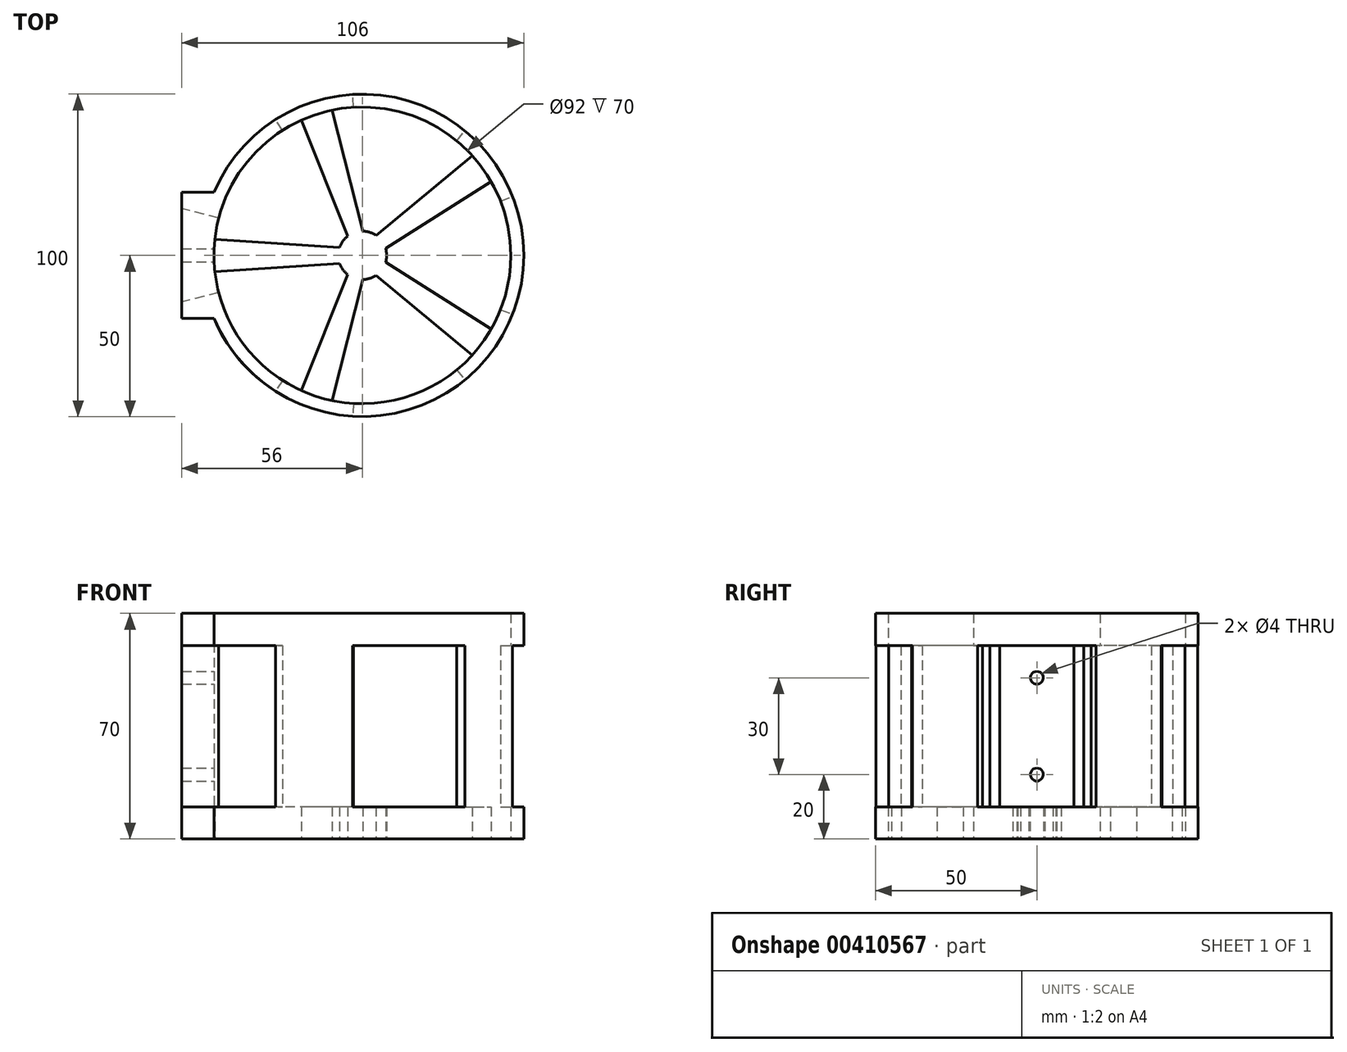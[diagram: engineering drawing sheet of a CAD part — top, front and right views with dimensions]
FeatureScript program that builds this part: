
annotation { "Feature Type Name" : "Feature", "Feature Type Description" : "" }
export const myFeature = defineFeature(function(context is Context, id is Id, definition is map)
    precondition{}
    {
        {
            var Q0;
            Q0=qCreatedBy(makeId("Top.planeOp"),FACE);
            var sketch = newSketch(context, id + "F0", { "sketchPlane" : qUnion([Q0])});
            skArc(sketch, "E0", {"start": v(-46, -19.6) * mm, "mid": v(50, 0) * mm, "end": v(-46, 19.6) * mm});
            skLineSegment(sketch, "E1", {"start": v(-46, -19.6) * mm, "end": v(-46, 19.6) * mm, "construction": true});
            skLineSegment(sketch, "E2", {"start": v(-46, 19.6) * mm, "end": v(-56, 19.6) * mm});
            skLineSegment(sketch, "E3", {"start": v(-46, -19.6) * mm, "end": v(-56, -19.6) * mm});
            skLineSegment(sketch, "E4", {"start": v(-56, -19.6) * mm, "end": v(-56, 19.6) * mm});
            skCircle(sketch, "E5", {"center": v(0, 0) * mm, "radius": 46 * mm});
            skSolve(sketch);
        }
        {
            var Q0;
            Q0=qSketchRegion(id+"F0",true);
            extrude(context, id + "F1", {"entities" : qUnion([Q0]), "depth" : 70 * mm});
        }
        {
            var Q0;
            Q0=makeQuery(id+"F1.opExtrude","CAP_FACE",FACE,{"disambiguationData":[OSD([sQuery(id+"F0.wireOp",EDGE,"E0"),sQuery(id+"F0.wireOp",EDGE,"E2"),sQuery(id+"F0.wireOp",EDGE,"E3"),sQuery(id+"F0.wireOp",EDGE,"E4"),sQuery(id+"F0.wireOp",EDGE,"E5")])],"isStart":true});
            var sketch = newSketch(context, id + "F2", { "sketchPlane" : qUnion([Q0])});
            skPoint(sketch, "E6", {"position": v(0, 0) * mm});
            skCircle(sketch, "E7", {"center": v(0, 0) * mm, "radius": 7.5 * mm});
            skLineSegment(sketch, "E8", {"start": v(-4.56, 5.95) * mm, "end": v(-18.89, 41.94) * mm});
            skLineSegment(sketch, "E9", {"start": v(0.2, 7.5) * mm, "end": v(-9.38, 45.03) * mm});
            skLineSegment(sketch, "E10", {"start": v(-18.89, 41.94) * mm, "end": v(-9.38, 45.03) * mm, "construction": true});
            skLineSegment(sketch, "E11", {"start": v(-4.56, 5.95) * mm, "end": v(0.2, 7.5) * mm, "construction": true});
            skLineSegment(sketch, "E12.1.0", {"start": v(-7.07, -2.5) * mm, "end": v(-45.73, -5) * mm});
            skLineSegment(sketch, "E12.1.1", {"start": v(-7.07, 2.5) * mm, "end": v(-45.73, 5) * mm});
            skLineSegment(sketch, "E12.1.2", {"start": v(-45.73, -5) * mm, "end": v(-45.73, 5) * mm, "construction": true});
            skLineSegment(sketch, "E12.1.3", {"start": v(-7.07, -2.5) * mm, "end": v(-7.07, 2.5) * mm, "construction": true});
            skLineSegment(sketch, "E12.2.0", {"start": v(0.2, -7.5) * mm, "end": v(-9.38, -45.03) * mm});
            skLineSegment(sketch, "E12.2.1", {"start": v(-4.56, -5.95) * mm, "end": v(-18.89, -41.94) * mm});
            skLineSegment(sketch, "E12.2.2", {"start": v(-9.38, -45.03) * mm, "end": v(-18.89, -41.94) * mm, "construction": true});
            skLineSegment(sketch, "E12.2.3", {"start": v(0.2, -7.5) * mm, "end": v(-4.56, -5.95) * mm, "construction": true});
            skLineSegment(sketch, "E13.1.3.0", {"start": v(7.2, -2.13) * mm, "end": v(39.93, -22.83) * mm});
            skLineSegment(sketch, "E13.3.3.0", {"start": v(4.25, -6.18) * mm, "end": v(34.06, -30.92) * mm});
            skLineSegment(sketch, "E13.6.3.0", {"start": v(39.93, -22.83) * mm, "end": v(34.06, -30.92) * mm, "construction": true});
            skLineSegment(sketch, "E13.9.3.0", {"start": v(7.2, -2.13) * mm, "end": v(4.25, -6.18) * mm, "construction": true});
            skLineSegment(sketch, "E13.1.4.0", {"start": v(4.25, 6.18) * mm, "end": v(34.06, 30.92) * mm});
            skLineSegment(sketch, "E13.3.4.0", {"start": v(7.2, 2.13) * mm, "end": v(39.93, 22.83) * mm});
            skLineSegment(sketch, "E13.6.4.0", {"start": v(34.06, 30.92) * mm, "end": v(39.93, 22.83) * mm, "construction": true});
            skLineSegment(sketch, "E13.9.4.0", {"start": v(4.25, 6.18) * mm, "end": v(7.2, 2.13) * mm, "construction": true});
            skSolve(sketch);
        }
        {
            var Q0;
            Q0=qSketchRegion(id+"F2",true);
            var Q1;
            {var subQ0=sQuery(id+"F2.wireOp",EDGE,"E12.1.0");Q1=makeQuery(id+"F2.imprint","IMPRINT",FACE,{"disambiguationData":[TD([[makeQuery(id+"F2.imprint","IMPRINT",EDGE,{"derivedFrom":subQ0}),-1.0]])]});}
            var Q2;
            {var subQ0=sQuery(id+"F2.wireOp",EDGE,"E8");Q2=makeQuery(id+"F2.imprint","IMPRINT",FACE,{"disambiguationData":[TD([[makeQuery(id+"F2.imprint","IMPRINT",EDGE,{"derivedFrom":subQ0}),-1.0]])]});}
            var Q3;
            {var subQ0=sQuery(id+"F2.wireOp",EDGE,"E13.1.4.0");Q3=makeQuery(id+"F2.imprint","IMPRINT",FACE,{"disambiguationData":[TD([[makeQuery(id+"F2.imprint","IMPRINT",EDGE,{"derivedFrom":subQ0}),-1.0]])]});}
            var Q4;
            {var subQ0=sQuery(id+"F2.wireOp",EDGE,"E13.1.3.0");Q4=makeQuery(id+"F2.imprint","IMPRINT",FACE,{"disambiguationData":[TD([[makeQuery(id+"F2.imprint","IMPRINT",EDGE,{"derivedFrom":subQ0}),-1.0]])]});}
            var Q5;
            {var subQ0=sQuery(id+"F2.wireOp",EDGE,"E12.2.0");Q5=makeQuery(id+"F2.imprint","IMPRINT",FACE,{"disambiguationData":[TD([[makeQuery(id+"F2.imprint","IMPRINT",EDGE,{"derivedFrom":subQ0}),-1.0]])]});}
            extrude(context, id + "F3", {"entities" : qUnion([Q0, Q1, Q2, Q3, Q4, Q5]), "operationType" : NewBodyOperationType.ADD, "oppositeDirection" : true, "depth" : 10 * mm});
        }
        {
            var Q0;
            Q0=makeQuery(id+"F3.opExtrude","CAP_FACE",FACE,{"disambiguationData":[OSD([sQuery(id+"F0.wireOp",EDGE,"E5"),sQuery(id+"F2.wireOp",EDGE,"E7"),sQuery(id+"F2.wireOp",EDGE,"E8"),sQuery(id+"F2.wireOp",EDGE,"E9"),sQuery(id+"F2.wireOp",EDGE,"E12.1.0"),sQuery(id+"F2.wireOp",EDGE,"E12.1.1"),sQuery(id+"F2.wireOp",EDGE,"E12.2.0"),sQuery(id+"F2.wireOp",EDGE,"E12.2.1"),sQuery(id+"F2.wireOp",EDGE,"E13.1.3.0"),sQuery(id+"F2.wireOp",EDGE,"E13.3.3.0"),sQuery(id+"F2.wireOp",EDGE,"E13.1.4.0"),sQuery(id+"F2.wireOp",EDGE,"E13.3.4.0")])],"isStart":false});
            cPlane(context, id + "F4", {"entities" : qUnion([Q0]), "cplaneType" : CPlaneType.OFFSET, "offset" : 0 * mm, "width" : 150 * mm, "height" : 150 * mm});
        }
        {
            var Q0;
            Q0=qCreatedBy(id+"F4.planeOp",FACE);
            var sketch = newSketch(context, id + "F5", { "sketchPlane" : qUnion([Q0])});
            skCircle(sketch, "E14", {"center": v(0, 0) * mm, "radius": 76.53 * mm, "construction": true});
            skCircle(sketch, "E15", {"center": v(0, 0) * mm, "radius": 46 * mm, "construction": true});
            skArc(sketch, "E16", {"start": v(42.8, -16.84) * mm, "mid": v(46, 0) * mm, "end": v(42.8, 16.84) * mm});
            skLineSegment(sketch, "E17", {"start": v(42.8, -16.84) * mm, "end": v(42.8, 16.84) * mm});
            skArc(sketch, "E18", {"start": v(71.22, -28) * mm, "mid": v(76.53, 0) * mm, "end": v(71.22, 28) * mm});
            skLineSegment(sketch, "E19", {"start": v(42.8, -16.84) * mm, "end": v(71.22, -28) * mm});
            skLineSegment(sketch, "E20", {"start": v(42.8, 16.84) * mm, "end": v(71.22, 28) * mm});
            skLineSegment(sketch, "E21", {"start": v(42.8, -16.84) * mm, "end": v(0, 0) * mm, "construction": true});
            skLineSegment(sketch, "E22", {"start": v(42.8, 16.84) * mm, "end": v(0, 0) * mm, "construction": true});
            skLineSegment(sketch, "E23.1.0", {"start": v(29.24, 35.51) * mm, "end": v(48.65, 59.08) * mm});
            skLineSegment(sketch, "E23.1.1", {"start": v(-2.78, 45.92) * mm, "end": v(-4.63, 76.39) * mm});
            skLineSegment(sketch, "E23.1.2", {"start": v(29.24, 35.51) * mm, "end": v(-2.78, 45.92) * mm});
            skArc(sketch, "E23.1.3", {"start": v(48.65, 59.08) * mm, "mid": v(23.65, 72.78) * mm, "end": v(-4.63, 76.39) * mm});
            skLineSegment(sketch, "E23.2.0", {"start": v(-24.74, 38.78) * mm, "end": v(-41.15, 64.52) * mm});
            skLineSegment(sketch, "E23.2.1", {"start": v(-44.53, 11.54) * mm, "end": v(-74.08, 19.2) * mm});
            skLineSegment(sketch, "E23.2.2", {"start": v(-24.74, 38.78) * mm, "end": v(-44.53, 11.54) * mm});
            skArc(sketch, "E23.2.3", {"start": v(-41.15, 64.52) * mm, "mid": v(-61.91, 44.98) * mm, "end": v(-74.08, 19.2) * mm});
            skLineSegment(sketch, "E24.1.3.0", {"start": v(-44.53, -11.54) * mm, "end": v(-74.08, -19.2) * mm});
            skLineSegment(sketch, "E24.3.3.0", {"start": v(-24.74, -38.78) * mm, "end": v(-41.15, -64.52) * mm});
            skLineSegment(sketch, "E24.6.3.0", {"start": v(-44.53, -11.54) * mm, "end": v(-24.74, -38.78) * mm});
            skArc(sketch, "E24.9.3.0", {"start": v(-74.08, -19.2) * mm, "mid": v(-61.91, -44.98) * mm, "end": v(-41.15, -64.52) * mm});
            skLineSegment(sketch, "E24.1.4.0", {"start": v(-2.78, -45.92) * mm, "end": v(-4.63, -76.39) * mm});
            skLineSegment(sketch, "E24.3.4.0", {"start": v(29.24, -35.51) * mm, "end": v(48.65, -59.08) * mm});
            skLineSegment(sketch, "E24.6.4.0", {"start": v(-2.78, -45.92) * mm, "end": v(29.24, -35.51) * mm});
            skArc(sketch, "E24.9.4.0", {"start": v(-4.63, -76.39) * mm, "mid": v(23.65, -72.78) * mm, "end": v(48.65, -59.08) * mm});
            skSolve(sketch);
        }
        {
            var Q0;
            Q0=qSketchRegion(id+"F5",true);
            extrude(context, id + "F6", {"entities" : qUnion([Q0]), "operationType" : NewBodyOperationType.REMOVE, "depth" : 50 * mm});
        }
        {
            var Q0;
            Q0=qCreatedBy(makeId("Right.planeOp"),FACE);
            var sketch = newSketch(context, id + "F7", { "sketchPlane" : qUnion([Q0])});
            skLineSegment(sketch, "E25", {"start": v(0, 0) * mm, "end": v(0, 42.9) * mm, "construction": true});
            skPoint(sketch, "E26", {"position": v(0, 21.45) * mm});
            skCircle(sketch, "E27", {"center": v(0, 50) * mm, "radius": 2 * mm});
            skCircle(sketch, "E28", {"center": v(0, 20) * mm, "radius": 2 * mm});
            skSolve(sketch);
        }
        {
            var Q0;
            Q0=qSketchRegion(id+"F7",true);
            extrude(context, id + "F8", {"entities" : qUnion([Q0]), "operationType" : NewBodyOperationType.REMOVE, "endBound" : BoundingType.THROUGH_ALL, "oppositeDirection" : true, "depth" : 25 * mm});
        }
    });
